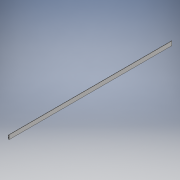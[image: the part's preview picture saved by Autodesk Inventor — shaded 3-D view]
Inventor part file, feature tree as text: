
AUTODESK INVENTOR PART (.ipt)
format: ipt  version: 2018 (Build 220112000, 112)  size: 120,320 bytes
history: native  units: mm
features: extrude x1
ambient origin geometry x8: Origin, YZ Plane, XZ Plane, XY Plane, X Axis, Y Axis, Z Axis, Center Point
bodies: Volumenkörper1 (feature_tree)
feature tree (1):
  extrude  "Extrusion1"  Depth=0.5mm
